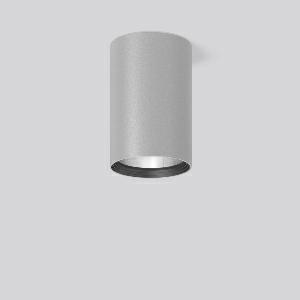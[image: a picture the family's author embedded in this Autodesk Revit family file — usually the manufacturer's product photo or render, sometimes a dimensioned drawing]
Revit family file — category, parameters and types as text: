
# Revit family: heledon_maxi_a_931224_004_2_76_5fdf
name_source: partatom
category: Lighting Fixtures
units: mm (PartAtom-declared; Revit-internal decimal feet)

## family parameters
Cut with Voids When Loaded = No
Host = Face
Light Source = No
Part Type = Normal
Room Calculation Point = No
Round Connector Dimension = Use Diameter
Shared = No

## types (1)
- HELEDON maxi A (1 x LED Modul 927, 4100 lm, 2700)
    Apparent Load = 35 VA
    Approval mark = CE
    CIE Flux Codes = 100 100 100 100 100
    Color Rendering = 92
    Color Temperature = 2700
    Default Elevation = 1800 mm
    Description = Series: HELEDON maxi
Cylindrical surface-mounted downlight. Housing: die-cast aluminium, powder-coated. Internal ceiling frame polycarbonate with bayonet mounting. Black plastic ring and recessed LED to prevent glare from the side. Optical assembly with reflector made of MIRO-Silver with 98% total light reflection for outstanding efficiency - can be changed without tools. Best colour rendering index Ra>90. Suitable for Ceiling mounting. Easy installation with a separate ceiling frame with bayonet mounting and plug connection. Driver integrated. Connected via plug-in connector. High quality converter without flickering and stroboscopic effect. The following accessories can be mounted without use of tools: interchangeable lenses, decorative glasses, honeycomb louvre, clear and frosted diffusers, white interchangeable plastic ring. 
Colour: silver
Diameter: 123 mm
Height: 183 mm
Lamp: LED
Socket: without socket
Colour temperature: 2700K
Colour rendering index (CRI): 92
System power: 35 W
Rated luminous flux: 4100 lm
Luminous efficiency: 117 lm/W
Control gear: Converter, dimmable, DALI
Protection class: I
Type of protection: IP 20
    Height = 183 mm
    Lamp = 1 x LED Modul 927
    Lamp Light Flux = 4100 lm
    Lamp count = 1
    Length = 123 mm
    Lifetime = 50000 h
    Luminous efficacy = 117 lm/W
    Manufacturer = RZB
    ModVariant = No
    Model = 931224.004.2.76
    Mounting Place = Ceiling
    Mounting Type = Surface mounted
    Number of Poles = 1
    OnlyDefault = Yes
    Power Factor = 1
    Product Name = HELEDON maxi A
    Product group = Surface mounted downlights
    ProductGroupID = 302
    Protection Class = Protection class I
    Protection Degree = IP 20
    RLX_Detail_Level = 1
    RLX_Emergency_Light_Flux = 0 lm
    RLX_Emergency_Type = 0
    RLX_Emergency_Type_DB = No
    RlxData = <blob elided: 100021 chars, md5=90d1aaa4>
    Socket = socket
    Standby Power = 0 W
    System Light Flux = 4100 lm
    System Power = 35 W
    Type Comments = Product without accessories
    Type Image = 931192.004.jpg
    URL = http://relux.com
    VarID = ---
    Voltage = 230 V
    Voltage Range = 220-240 V
    Weight = 0.00 kg
    Width = 0 mm  [stored 0 ft]

note: [stored X ft] marks values corroborated as IEEE doubles in the binary element streams (Revit-internal decimal feet)

## geometry (parser evidence)
native form markers: Blend x4, Sweep x11
no freeform markers — native parametric forms only
